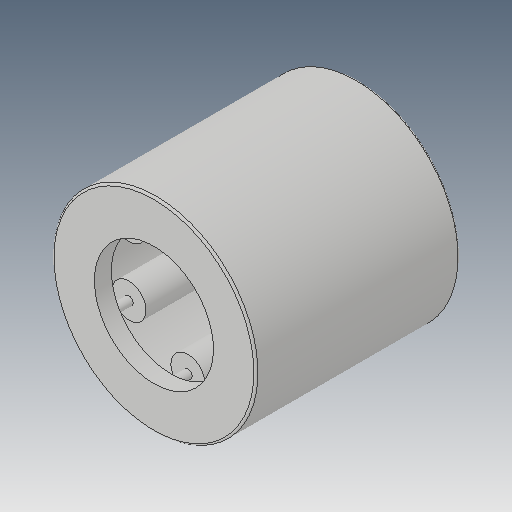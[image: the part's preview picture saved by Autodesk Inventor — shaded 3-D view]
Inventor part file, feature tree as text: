
AUTODESK INVENTOR PART (.ipt)
format: ipt  version: 2018 (Build 220112000, 112)  size: 188,928 bytes
history: native  units: in
note: dims shown in document units (in); Inventor stores cm internally (conversion verified against a paired STEP export)
features: other x10, revolve x2, fillet x1
ambient origin geometry x8: Origin, YZ Plane, XZ Plane, XY Plane, X Axis, Y Axis, Z Axis, Center Point
bodies: Solid1 (feature_tree), Solid2 (feature_tree), Solid3 (feature_tree), Solid4 (feature_tree), Solid5 (feature_tree), Solid6 (feature_tree), Solid7 (feature_tree), Solid8 (feature_tree), Solid9 (feature_tree), Solid10 (feature_tree), Solid11 (feature_tree), Solid12 (feature_tree), Solid13 (feature_tree)
feature tree (13):
  fillet  "Fillet1"  [1 undecoded]
  revolve  "Revolve2"  [1 undecoded]
  revolve  "Revolve3"  [1 undecoded]
  other  "CirPattern1[1]"
  other  "CirPattern1[2]"
  other  "CirPattern1[3]"
  other  "CirPattern1[4]"
  other  "CirPattern1[5]"
  other  "CirPattern1[6]"
  other  "CirPattern1[7]"
  other  "CirPattern1[8]"
  other  "CirPattern1[9]"
  other  "CirPattern1[10]"
note: 3 required parameter values undecoded (feature->parameter linkage not recoverable at this tier; creation-order binding heuristic only, values carry confidence <= 0.55)
